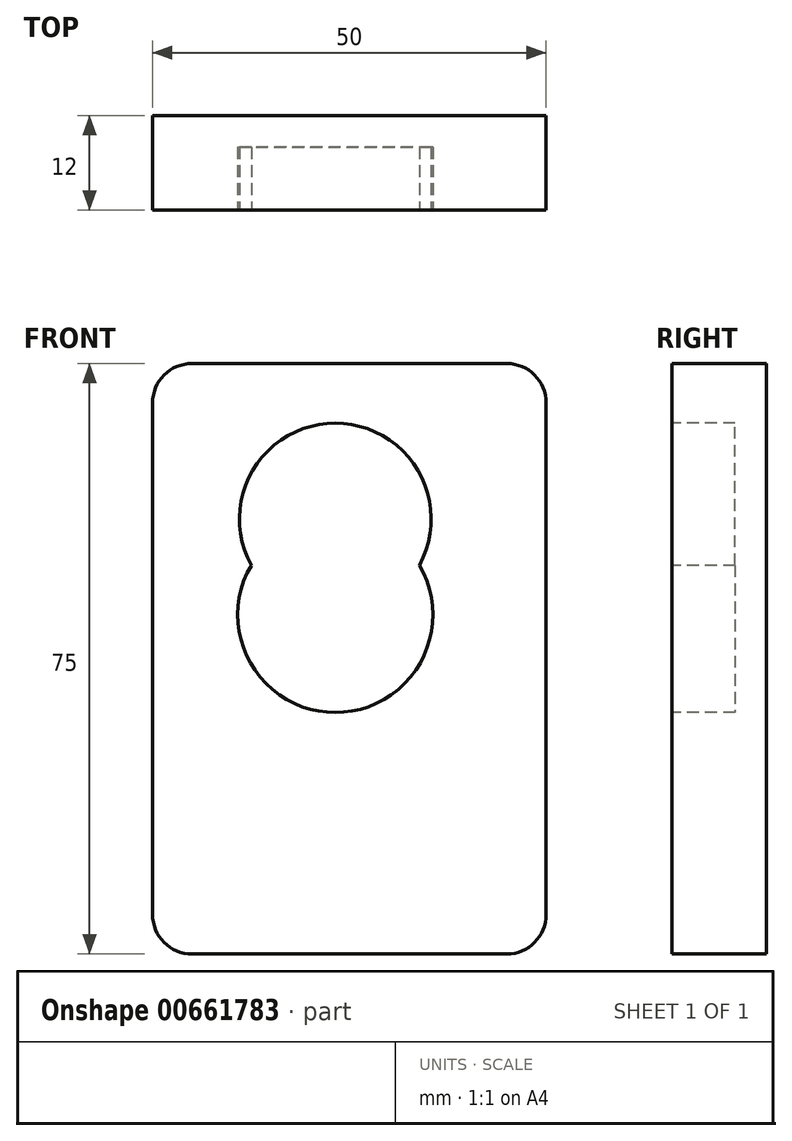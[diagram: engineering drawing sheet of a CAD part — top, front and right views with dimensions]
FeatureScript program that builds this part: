
annotation { "Feature Type Name" : "Feature", "Feature Type Description" : "" }
export const myFeature = defineFeature(function(context is Context, id is Id, definition is map)
    precondition{}
    {
        {
            var Q0;
            Q0=qCreatedBy(makeId("Front.planeOp"),FACE);
            var sketch = newSketch(context, id + "F0", { "sketchPlane" : qUnion([Q0])});
            skLineSegment(sketch, "E0.bottom", {"start": v(0, 0) * mm, "end": v(50, 0) * mm});
            skLineSegment(sketch, "E0.top", {"start": v(0, 75) * mm, "end": v(50, 75) * mm});
            skLineSegment(sketch, "E0.left", {"start": v(0, 0) * mm, "end": v(0, 75) * mm});
            skLineSegment(sketch, "E0.right", {"start": v(50, 0) * mm, "end": v(50, 75) * mm});
            skSolve(sketch);
        }
        {
            var Q0;
            Q0 = qSketchRegion(id + "F0", true);
            extrude(context, id + "F1", {"entities" : qUnion([Q0]), "depth" : 12 * mm, "offsetDistance" : 25 * mm});
        }
        {
            var Q0;
            Q0=makeQuery(id+"F1.opExtrude","CAP_FACE",FACE,{"disambiguationData":[OSD([sQuery(id+"F0.wireOp",EDGE,"E0.bottom"),sQuery(id+"F0.wireOp",EDGE,"E0.top"),sQuery(id+"F0.wireOp",EDGE,"E0.left"),sQuery(id+"F0.wireOp",EDGE,"E0.right")])],"isStart":false});
            var sketch = newSketch(context, id + "F2", { "sketchPlane" : qUnion([Q0])});
            skArc(sketch, "E1", {"start": v(33.88, 49.37) * mm, "mid": v(23.21, 67.42) * mm, "end": v(12.55, 49.37) * mm});
            skArc(sketch, "E2", {"start": v(12.55, 49.37) * mm, "mid": v(23.21, 30.67) * mm, "end": v(33.88, 49.37) * mm});
            skSolve(sketch);
        }
        {
            var Q0;
            Q0=makeQuery(id+"F2.imprint","IMPRINT",FACE,{"disambiguationData":[TD([[makeQuery(id+"F2.imprint","IMPRINT",EDGE,{"derivedFrom":sQuery(id+"F2.wireOp",EDGE,"E1")}),1.0]])]});
            extrude(context, id + "F3", {"entities" : qUnion([Q0]), "operationType" : NewBodyOperationType.REMOVE, "oppositeDirection" : true, "depth" : 8 * mm, "offsetDistance" : 25 * mm});
        }
        {
            var Q0;
            Q0=makeQuery(id+"F1.opExtrude","SWEPT_EDGE",EDGE,{"disambiguationData":[OSD([sQuery(id+"F0.wireOp",EDGE,"E0.bottom"),sQuery(id+"F0.wireOp",EDGE,"E0.right")])]});
            var Q1;
            Q1=makeQuery(id+"F1.opExtrude","SWEPT_EDGE",EDGE,{"disambiguationData":[OSD([sQuery(id+"F0.wireOp",EDGE,"E0.top"),sQuery(id+"F0.wireOp",EDGE,"E0.right")])]});
            var Q2;
            Q2=makeQuery(id+"F1.opExtrude","SWEPT_EDGE",EDGE,{"disambiguationData":[OSD([sQuery(id+"F0.wireOp",EDGE,"E0.top"),sQuery(id+"F0.wireOp",EDGE,"E0.left")])]});
            var Q3;
            Q3=makeQuery(id+"F1.opExtrude","SWEPT_EDGE",EDGE,{"disambiguationData":[OSD([sQuery(id+"F0.wireOp",EDGE,"E0.bottom"),sQuery(id+"F0.wireOp",EDGE,"E0.left")])]});
            fillet(context, id + "F4", {"entities" : qUnion([Q0, Q1, Q2, Q3]), "radius" : 5 * mm, "tangentPropagation" : true, "allowEdgeOverflow" : false});
        }
    });
